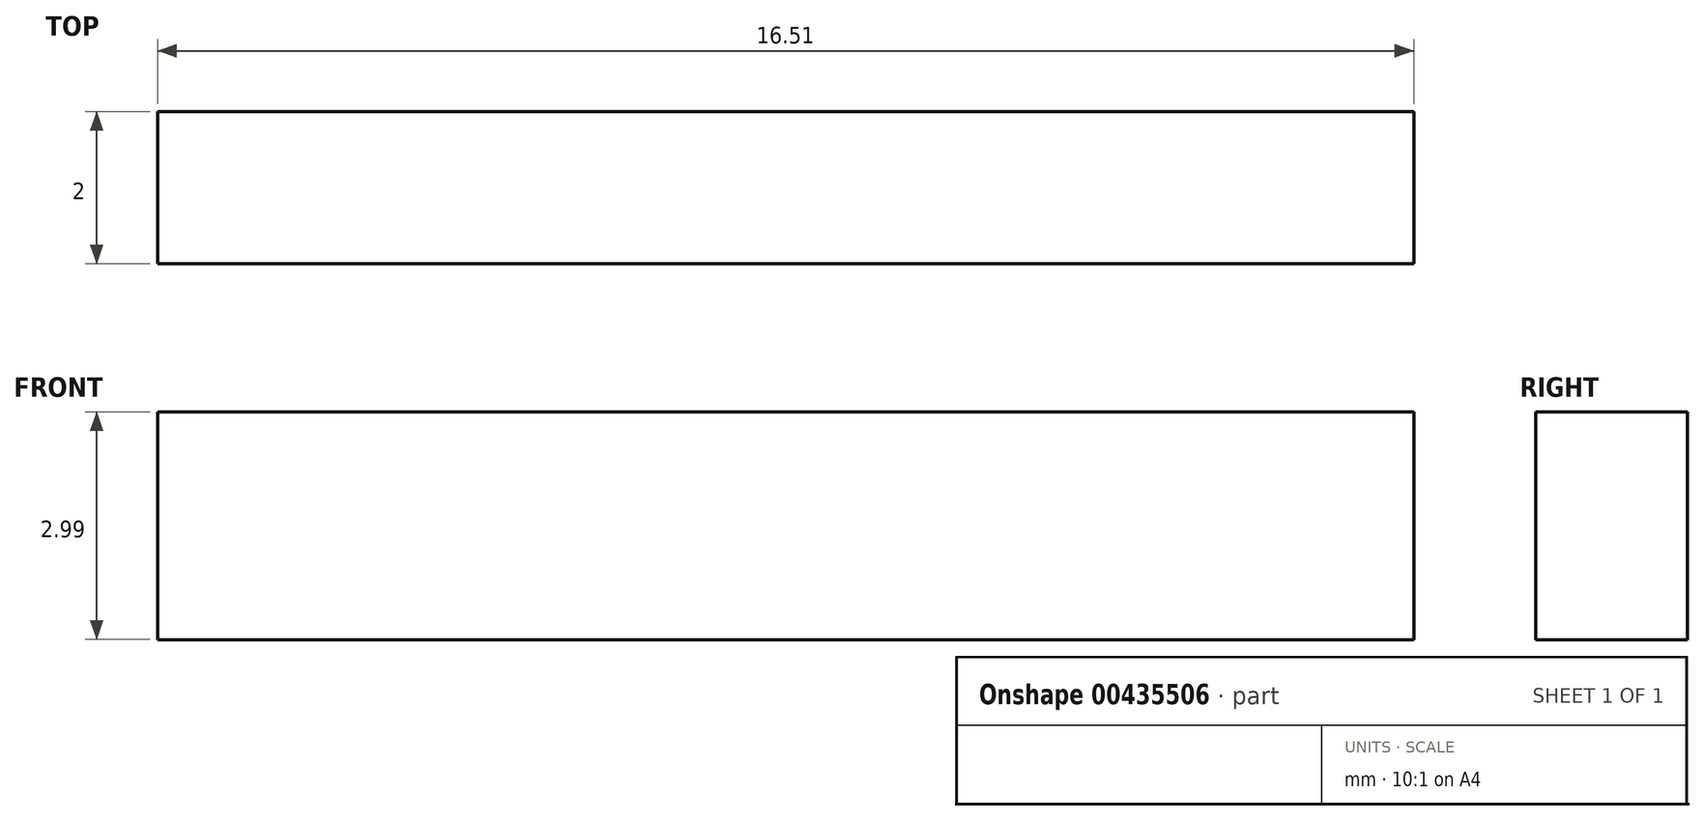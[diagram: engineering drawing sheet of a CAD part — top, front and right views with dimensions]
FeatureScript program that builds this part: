
annotation { "Feature Type Name" : "Feature", "Feature Type Description" : "" }
export const myFeature = defineFeature(function(context is Context, id is Id, definition is map)
    precondition{}
    {
        {
            var Q0;
            Q0=qCreatedBy(makeId("Front.planeOp"),FACE);
            var sketch = newSketch(context, id + "F0", { "sketchPlane" : qUnion([Q0])});
            skLineSegment(sketch, "E0.bottom", {"start": v(-3.24, 1.8) * mm, "end": v(13.27, 1.8) * mm});
            skLineSegment(sketch, "E0.top", {"start": v(-3.24, -1.2) * mm, "end": v(13.27, -1.2) * mm});
            skLineSegment(sketch, "E0.left", {"start": v(-3.24, 1.8) * mm, "end": v(-3.24, -1.2) * mm});
            skLineSegment(sketch, "E0.right", {"start": v(13.27, 1.8) * mm, "end": v(13.27, -1.2) * mm});
            skSolve(sketch);
        }
        {
            var Q0;
            Q0=makeQuery(id+"F0.imprint","IMPRINT",FACE,{"disambiguationData":[TD([[makeQuery(id+"F0.imprint","IMPRINT",EDGE,{"derivedFrom":sQuery(id+"F0.wireOp",EDGE,"E0.bottom")}),-1.0]])]});
            extrude(context, id + "F1", {"entities" : qUnion([Q0]), "depth" : 2 * mm});
        }
    });
